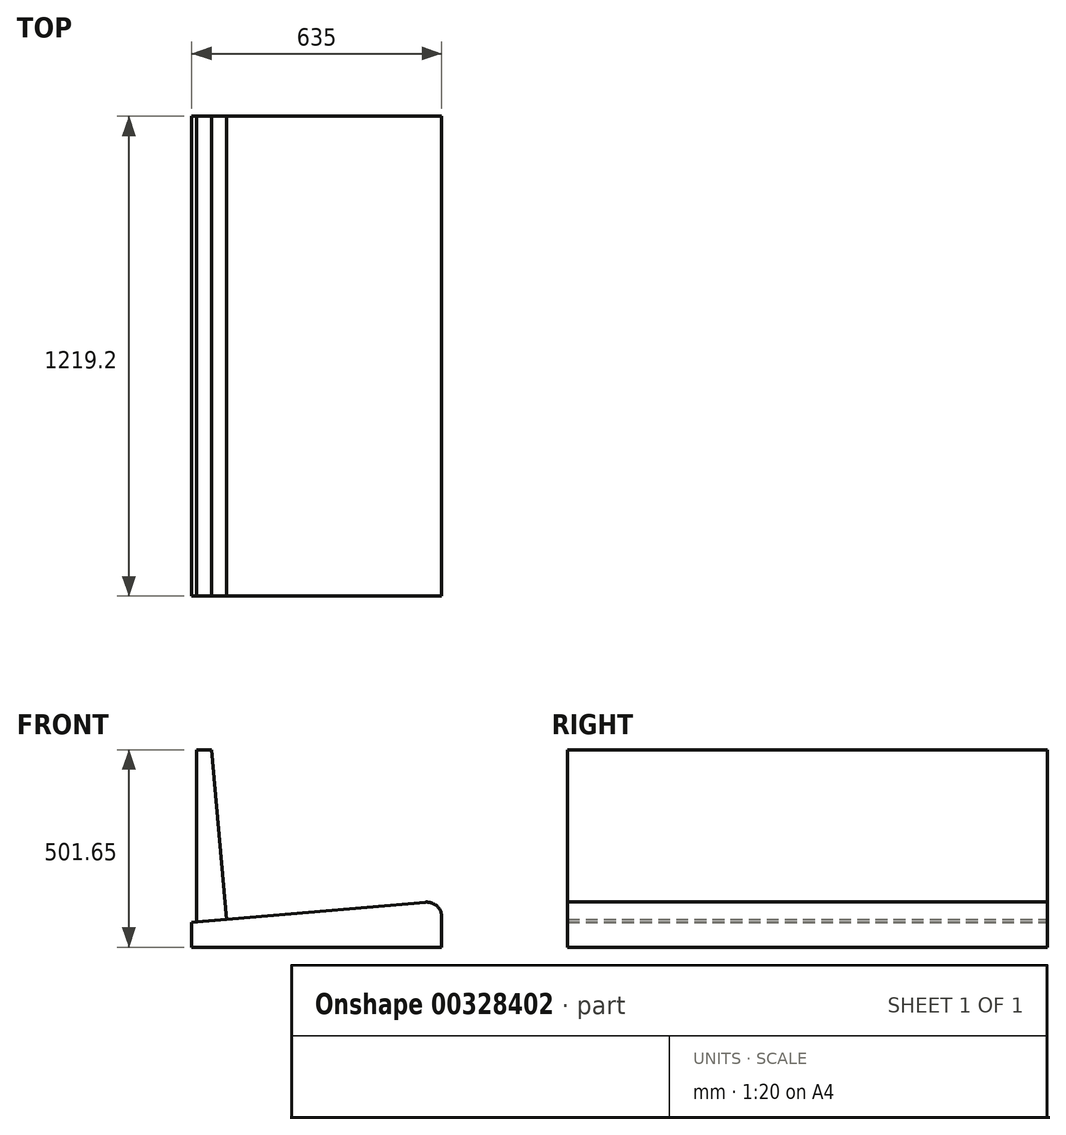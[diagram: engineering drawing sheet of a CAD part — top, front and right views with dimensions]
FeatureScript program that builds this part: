
annotation { "Feature Type Name" : "Feature", "Feature Type Description" : "" }
export const myFeature = defineFeature(function(context is Context, id is Id, definition is map)
    precondition{}
    {
        {
            var Q0;
            Q0=qCreatedBy(makeId("Front.planeOp"),FACE);
            var sketch = newSketch(context, id + "F0", { "sketchPlane" : qUnion([Q0])});
            skLineSegment(sketch, "E0", {"start": v(0, 0) * mm, "end": v(0, 514.35) * mm});
            skLineSegment(sketch, "E1", {"start": v(0, 0) * mm, "end": v(587.38, 0) * mm});
            skLineSegment(sketch, "E2", {"start": v(0, 514.35) * mm, "end": v(12.7, 514.35) * mm});
            skLineSegment(sketch, "E3", {"start": v(12.7, 514.35) * mm, "end": v(12.7, 533.4) * mm});
            skLineSegment(sketch, "E4", {"start": v(12.7, 533.4) * mm, "end": v(-63.5, 533.4) * mm});
            skLineSegment(sketch, "E5", {"start": v(587.38, 0) * mm, "end": v(587.38, -101.6) * mm});
            skSolve(sketch);
        }
        {
            var Q0;
            Q0=qCreatedBy(makeId("Front.planeOp"),FACE);
            var sketch = newSketch(context, id + "F1", { "sketchPlane" : qUnion([Q0])});
            skLineSegment(sketch, "E6.bottom", {"start": v(3.17, 12.7) * mm, "end": v(622.3, 12.7) * mm});
            skLineSegment(sketch, "E6.top", {"start": v(3.17, 0) * mm, "end": v(622.3, 0) * mm});
            skLineSegment(sketch, "E6.left", {"start": v(3.17, 12.7) * mm, "end": v(3.17, 0) * mm});
            skLineSegment(sketch, "E6.right", {"start": v(622.3, 12.7) * mm, "end": v(622.3, 0) * mm});
            skLineSegment(sketch, "E7", {"start": v(0, 12.7) * mm, "end": v(635, 12.7) * mm});
            skLineSegment(sketch, "E8", {"start": v(635, 12.7) * mm, "end": v(635, 89.04) * mm});
            skArc(sketch, "E9", {"start": v(635, 89.04) * mm, "mid": v(622.67, 117.1) * mm, "end": v(593.65, 127) * mm});
            skLineSegment(sketch, "E10", {"start": v(593.65, 127) * mm, "end": v(0, 76.2) * mm});
            skLineSegment(sketch, "E11", {"start": v(0, 76.2) * mm, "end": v(0, 12.7) * mm});
            skLineSegment(sketch, "E12.bottom", {"start": v(0, 511.18) * mm, "end": v(12.7, 511.18) * mm});
            skLineSegment(sketch, "E12.top", {"start": v(0, 79.38) * mm, "end": v(12.7, 79.38) * mm});
            skLineSegment(sketch, "E12.left", {"start": v(0, 511.18) * mm, "end": v(0, 79.38) * mm});
            skLineSegment(sketch, "E12.right", {"start": v(12.7, 511.18) * mm, "end": v(12.7, 79.38) * mm});
            skLineSegment(sketch, "E13", {"start": v(12.7, 511.18) * mm, "end": v(12.7, 514.35) * mm});
            skLineSegment(sketch, "E14", {"start": v(12.7, 514.35) * mm, "end": v(50.8, 514.35) * mm});
            skLineSegment(sketch, "E15", {"start": v(12.7, 79.38) * mm, "end": v(12.7, 77.29) * mm});
            skLineSegment(sketch, "E16", {"start": v(12.7, 77.29) * mm, "end": v(88.9, 83.8) * mm});
            skLineSegment(sketch, "E17", {"start": v(88.9, 83.8) * mm, "end": v(50.8, 514.35) * mm});
            skLineSegment(sketch, "E18.bottom", {"start": v(587.38, -101.6) * mm, "end": v(593.73, -101.6) * mm});
            skLineSegment(sketch, "E18.top", {"start": v(587.38, -3.18) * mm, "end": v(593.73, -3.18) * mm});
            skLineSegment(sketch, "E18.left", {"start": v(587.38, -101.6) * mm, "end": v(587.38, -3.17) * mm});
            skLineSegment(sketch, "E18.right", {"start": v(593.73, -101.6) * mm, "end": v(593.73, -3.17) * mm});
            skSolve(sketch);
        }
        {
            var Q0;
            {var subQ0=sQuery(id+"F1.wireOp",EDGE,"E8");Q0=makeQuery(id+"F1.imprint","IMPRINT",FACE,{"disambiguationData":[TD([[makeQuery(id+"F1.imprint","IMPRINT",EDGE,{"derivedFrom":subQ0}),1.0]])]});}
            extrude(context, id + "F2", {"entities" : qUnion([Q0]), "depth" : 1219.2 * mm});
        }
        {
            var Q0;
            Q0=makeQuery(id+"F1.imprint","IMPRINT",FACE,{"disambiguationData":[TD([[makeQuery(id+"F1.imprint","IMPRINT",EDGE,{"derivedFrom":sQuery(id+"F1.wireOp",EDGE,"E12.right")}),1.0]])]});
            extrude(context, id + "F3", {"entities" : qUnion([Q0]), "depth" : 1219.2 * mm});
        }
    });
